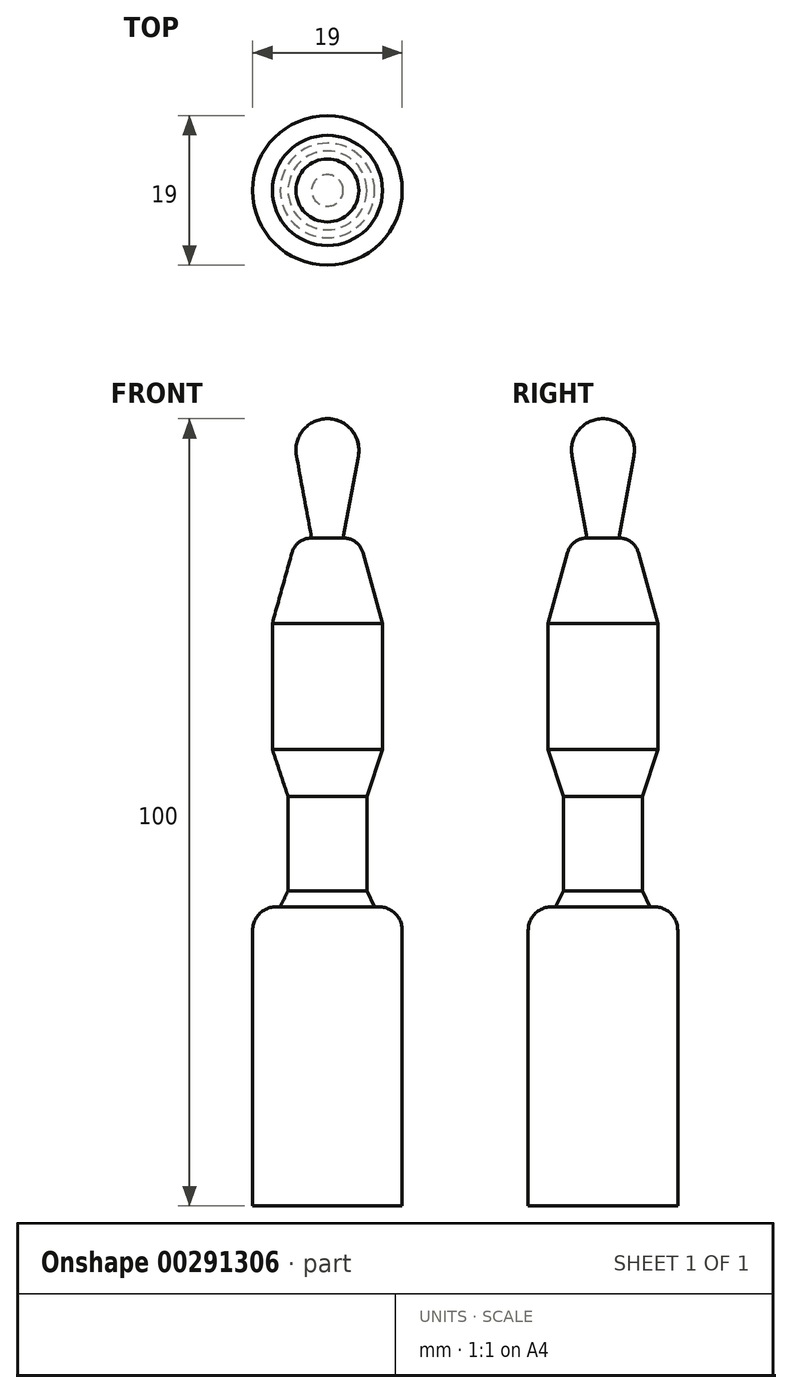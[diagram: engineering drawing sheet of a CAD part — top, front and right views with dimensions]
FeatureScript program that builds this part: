
annotation { "Feature Type Name" : "Feature", "Feature Type Description" : "" }
export const myFeature = defineFeature(function(context is Context, id is Id, definition is map)
    precondition{}
    {
        {
            var Q0;
            Q0=qCreatedBy(makeId("Front.planeOp"),FACE);
            var sketch = newSketch(context, id + "F0", { "sketchPlane" : qUnion([Q0])});
            skArc(sketch, "E0", {"start": v(3.93, -4.73) * mm, "mid": v(3.08, -1.44) * mm, "end": v(0, 0) * mm});
            skLineSegment(sketch, "E1", {"start": v(3.93, -4.73) * mm, "end": v(2, -15.17) * mm});
            skArc(sketch, "E2", {"start": v(4.5, -17) * mm, "mid": v(3.57, -15.65) * mm, "end": v(2, -15.17) * mm});
            skLineSegment(sketch, "E3", {"start": v(4.5, -17) * mm, "end": v(7, -26) * mm});
            skLineSegment(sketch, "E4", {"start": v(7, -26) * mm, "end": v(7, -42) * mm});
            skLineSegment(sketch, "E5", {"start": v(7, -42) * mm, "end": v(5, -48) * mm});
            skLineSegment(sketch, "E6", {"start": v(5, -48) * mm, "end": v(5, -60) * mm});
            skLineSegment(sketch, "E7", {"start": v(5, -60) * mm, "end": v(6, -62) * mm});
            skLineSegment(sketch, "E8", {"start": v(6, -62) * mm, "end": v(6.5, -62) * mm});
            skArc(sketch, "E9", {"start": v(9.5, -65) * mm, "mid": v(8.62, -62.88) * mm, "end": v(6.5, -62) * mm});
            skLineSegment(sketch, "E10", {"start": v(9.5, -65) * mm, "end": v(9.5, -100) * mm});
            skLineSegment(sketch, "E11", {"start": v(9.5, -100) * mm, "end": v(0, -100) * mm});
            skLineSegment(sketch, "E12", {"start": v(0, -100) * mm, "end": v(0, 0) * mm});
            skSolve(sketch);
        }
        {
            var Q0;
            Q0=makeQuery(id+"F0.imprint","IMPRINT",FACE,{"disambiguationData":[TD([[makeQuery(id+"F0.imprint","IMPRINT",EDGE,{"derivedFrom":sQuery(id+"F0.wireOp",EDGE,"E0")}),1.0]])]});
            var Q1;
            Q1=sQuery(id+"F0.wireOp",EDGE,"E12");
            revolve(context, id + "F1", {"entities" : qUnion([Q0]), "axis" : qUnion([Q1]), "revolveType" : RevolveType.FULL});
        }
    });
